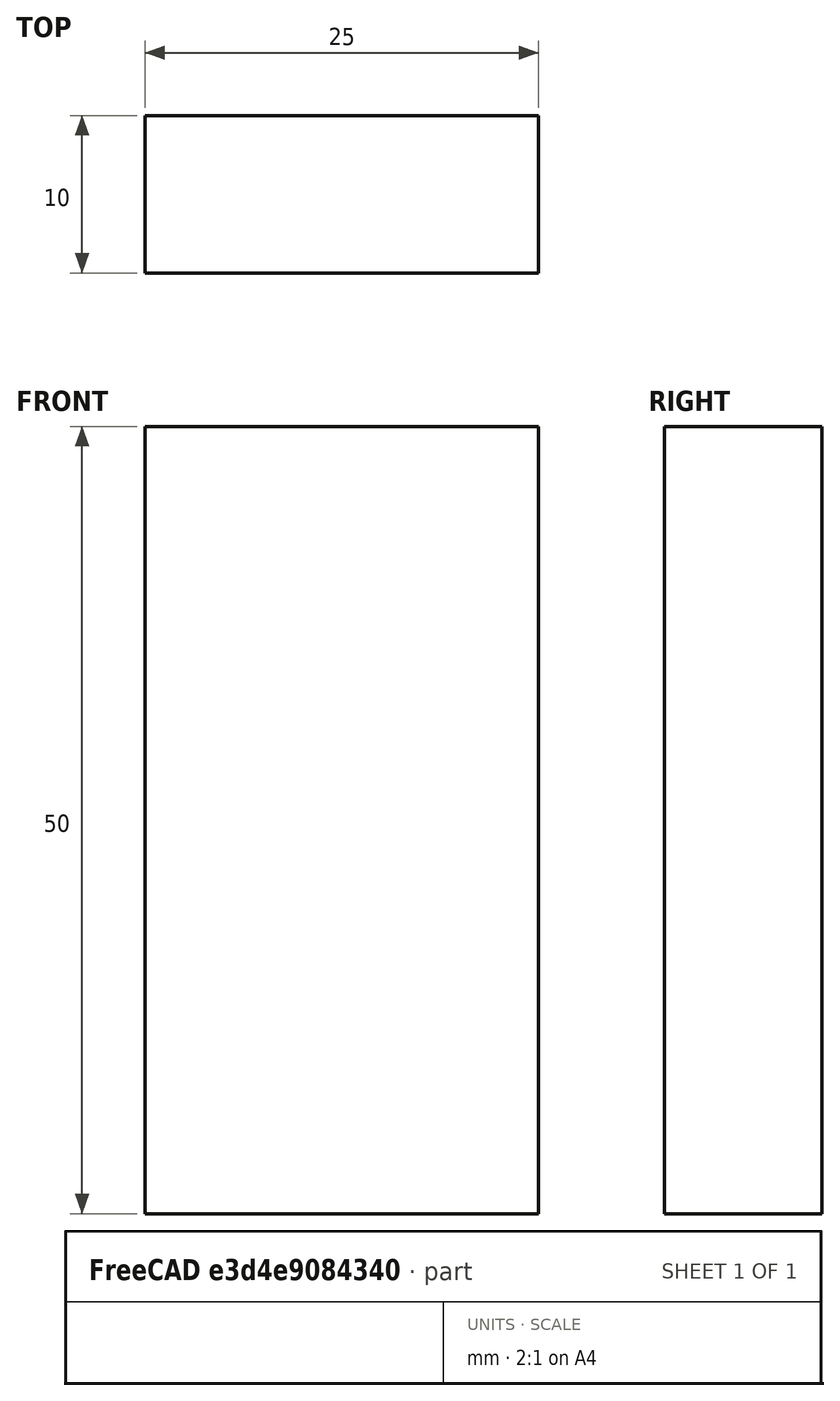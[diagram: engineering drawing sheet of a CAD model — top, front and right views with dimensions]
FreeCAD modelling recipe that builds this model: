
FCSTD DOCUMENT  (FreeCAD 0.15R4671 (Git))
Label: Flat Bar 25x10 EN10058 S235JR
License: All rights reserved
LicenseURL: http://en.wikipedia.org/wiki/All_rights_reserved
objects: Sketcher::SketchObject×1, Part::Extrusion×1
note: 2 computed .brp shape members not serialized (recipe doc carries the construction recipe); baked Part::Feature solids carry a one-line shape summary decoded from their .brp

FEATURE [Sketcher::SketchObject] Sketch
  sketch-geometry (4):
    g0: LineSegment StartX=-12.5 StartY=-5 StartZ=0 EndX=12.5 EndY=-5 EndZ=0
    g1: LineSegment StartX=12.5 StartY=-5 StartZ=0 EndX=12.5 EndY=5 EndZ=0
    g2: LineSegment StartX=12.5 StartY=5 StartZ=0 EndX=-12.5 EndY=5 EndZ=0
    g3: LineSegment StartX=-12.5 StartY=5 StartZ=0 EndX=-12.5 EndY=-5 EndZ=0
  constraints (12):
    c: Coincident(g0,g1)
    c: Coincident(g1,g2)
    c: Coincident(g2,g3)
    c: Coincident(g3,g0)
    c: Horizontal(g0)
    c: Horizontal(g2)
    c: Vertical(g1)
    c: Vertical(g3)
    c: Symmetric(g1,g2,g-2)
    c: Symmetric(g0,g1,g-1)
    c: DistanceY(g1) = 10
    c: DistanceX(g0) = 25
FEATURE [Part::Extrusion] Extrude  label="Flat Bar 25x10 EN10058 S235JR"
  Base = -> Sketch
  Dir = (0,0,50)
  Solid = true
